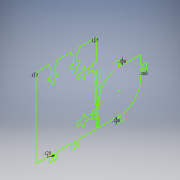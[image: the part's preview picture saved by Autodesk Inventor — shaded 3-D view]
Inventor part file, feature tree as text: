
AUTODESK INVENTOR PART (.ipt)
format: ipt  version: 2016 (Build 200138000, 138)  size: 137,216 bytes
history: native  units: in
note: dims shown in document units (in); Inventor stores cm internally (conversion verified against a paired STEP export)
features: sketch x1
ambient origin geometry x8: Origin, YZ Plane, XZ Plane, XY Plane, X Axis, Y Axis, Z Axis, Center Point
feature tree (1):
  sketch  "Sketch1"  dims[d30=0.12in d36=0.117in d68=0.117in d73=0.2in d74=0.2in d75=0.2in]
